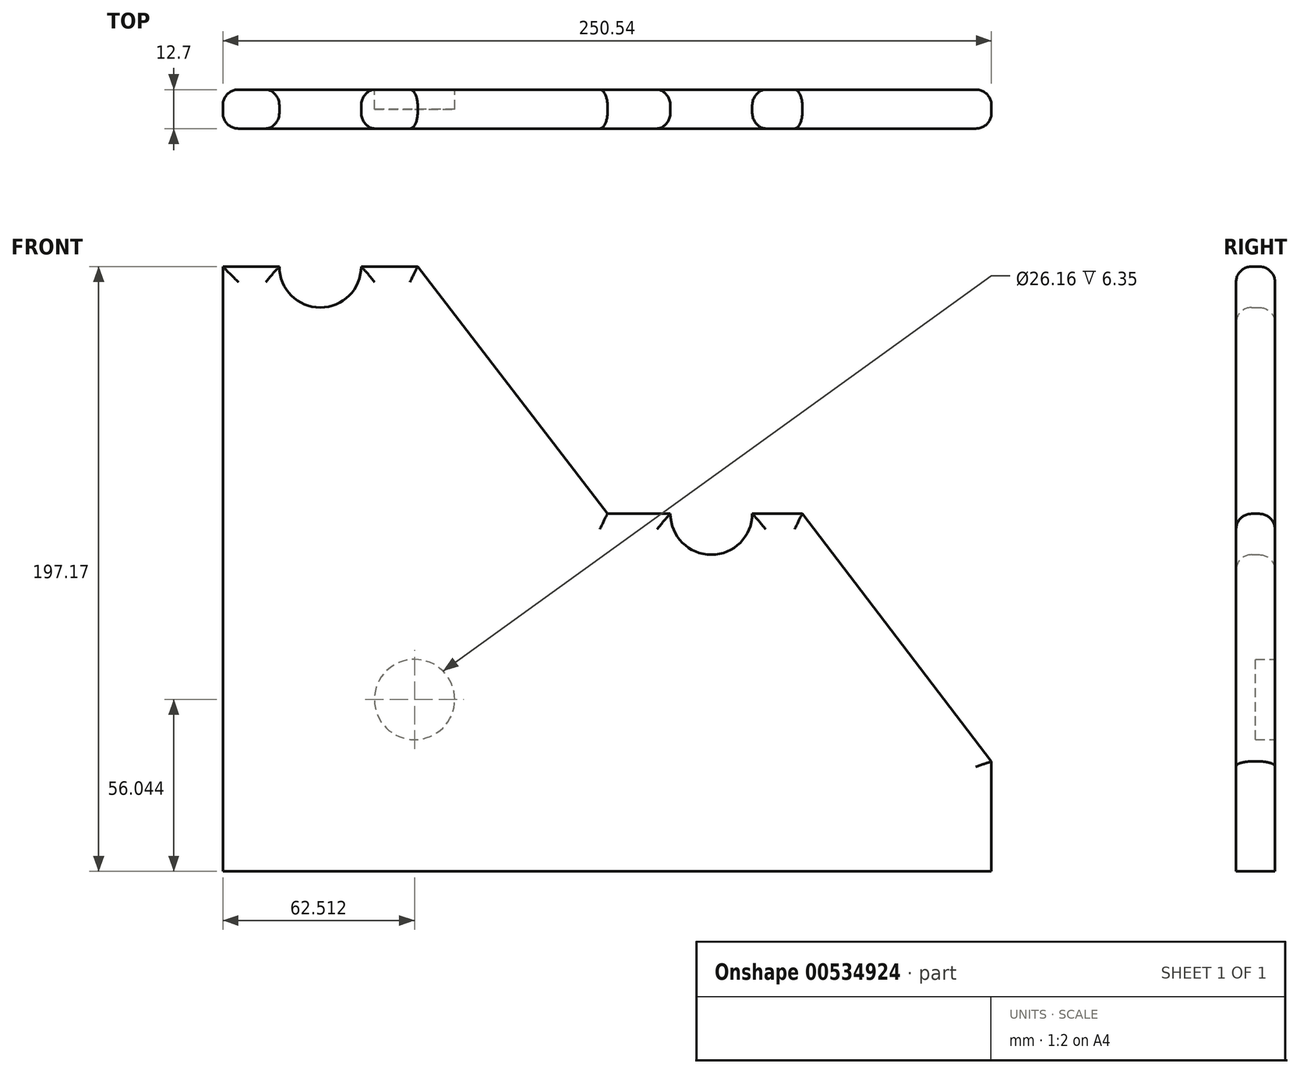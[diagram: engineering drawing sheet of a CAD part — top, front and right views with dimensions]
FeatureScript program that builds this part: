
annotation { "Feature Type Name" : "Feature", "Feature Type Description" : "" }
export const myFeature = defineFeature(function(context is Context, id is Id, definition is map)
    precondition{}
    {
        {
            var Q0;
            Q0=qCreatedBy(makeId("Front.planeOp"),FACE);
            var sketch = newSketch(context, id + "F0", { "sketchPlane" : qUnion([Q0])});
            skLineSegment(sketch, "E0", {"start": v(0, 0) * mm, "end": v(250.54, 0) * mm});
            skLineSegment(sketch, "E1", {"start": v(250.54, 0) * mm, "end": v(250.54, 41.87) * mm});
            skLineSegment(sketch, "E2", {"start": v(250.54, 41.87) * mm, "end": v(188.86, 122.6) * mm});
            skLineSegment(sketch, "E3", {"start": v(188.86, 122.6) * mm, "end": v(172.56, 122.6) * mm});
            skLineSegment(sketch, "E4", {"start": v(125.36, 122.6) * mm, "end": v(63.5, 203.2) * mm});
            skLineSegment(sketch, "E5", {"start": v(63.5, 203.2) * mm, "end": v(45.09, 203.2) * mm});
            skLineSegment(sketch, "E6", {"start": v(0, 203.2) * mm, "end": v(0, 0) * mm});
            skArc(sketch, "E7", {"start": v(145.9, 122.6) * mm, "mid": v(159.23, 109.27) * mm, "end": v(172.56, 122.6) * mm});
            skArc(sketch, "E8", {"start": v(18.41, 203.2) * mm, "mid": v(31.75, 189.86) * mm, "end": v(45.09, 203.2) * mm});
            skLineSegment(sketch, "E9.trimOffspring", {"start": v(18.41, 203.2) * mm, "end": v(0, 203.2) * mm});
            skLineSegment(sketch, "E10.trimOffspring", {"start": v(145.9, 122.6) * mm, "end": v(125.36, 122.6) * mm});
            skSolve(sketch);
        }
        {
            var Q0;
            Q0=makeQuery(id+"F0.imprint","IMPRINT",FACE,{"disambiguationData":[TD([[makeQuery(id+"F0.imprint","IMPRINT",EDGE,{"derivedFrom":sQuery(id+"F0.wireOp",EDGE,"E0")}),1.0]])]});
            extrude(context, id + "F1", {"entities" : qUnion([Q0]), "depth" : 12.7 * mm, "offsetDistance" : 25.4 * mm});
        }
        {
            var Q0;
            Q0=makeQuery(id+"F1.opExtrude","CAP_FACE",FACE,{"disambiguationData":[OSD([sQuery(id+"F0.wireOp",EDGE,"E0"),sQuery(id+"F0.wireOp",EDGE,"E1"),sQuery(id+"F0.wireOp",EDGE,"E2"),sQuery(id+"F0.wireOp",EDGE,"E3"),sQuery(id+"F0.wireOp",EDGE,"E4"),sQuery(id+"F0.wireOp",EDGE,"E5"),sQuery(id+"F0.wireOp",EDGE,"E6"),sQuery(id+"F0.wireOp",EDGE,"E7"),sQuery(id+"F0.wireOp",EDGE,"E8"),sQuery(id+"F0.wireOp",EDGE,"E9.trimOffspring"),sQuery(id+"F0.wireOp",EDGE,"E10.trimOffspring")])],"isStart":false});
            var Q1;
            Q1=makeQuery(id+"F1.opExtrude","CAP_FACE",FACE,{"disambiguationData":[OSD([sQuery(id+"F0.wireOp",EDGE,"E0"),sQuery(id+"F0.wireOp",EDGE,"E1"),sQuery(id+"F0.wireOp",EDGE,"E2"),sQuery(id+"F0.wireOp",EDGE,"E3"),sQuery(id+"F0.wireOp",EDGE,"E4"),sQuery(id+"F0.wireOp",EDGE,"E5"),sQuery(id+"F0.wireOp",EDGE,"E6"),sQuery(id+"F0.wireOp",EDGE,"E7"),sQuery(id+"F0.wireOp",EDGE,"E8"),sQuery(id+"F0.wireOp",EDGE,"E9.trimOffspring"),sQuery(id+"F0.wireOp",EDGE,"E10.trimOffspring")])],"isStart":true});
            fillet(context, id + "F2", {"entities" : qUnion([Q0, Q1]), "radius" : 5.08 * mm, "tangentPropagation" : true, "allowEdgeOverflow" : false});
        }
        {
            var Q0;
            Q0=qCreatedBy(makeId("Front.planeOp"),FACE);
            var sketch = newSketch(context, id + "F3", { "sketchPlane" : qUnion([Q0])});
            skLineSegment(sketch, "E11.bottom", {"start": v(-108.62, 6.03) * mm, "end": v(293.7, 6.03) * mm});
            skLineSegment(sketch, "E11.top", {"start": v(-108.62, -19.59) * mm, "end": v(293.7, -19.59) * mm});
            skLineSegment(sketch, "E11.left", {"start": v(-108.62, 6.03) * mm, "end": v(-108.62, -19.59) * mm});
            skLineSegment(sketch, "E11.right", {"start": v(293.7, 6.03) * mm, "end": v(293.7, -19.59) * mm});
            skSolve(sketch);
        }
        {
            var Q0;
            Q0=makeQuery(id+"F3.imprint","IMPRINT",FACE,{"disambiguationData":[TD([[makeQuery(id+"F3.imprint","IMPRINT",EDGE,{"derivedFrom":sQuery(id+"F3.wireOp",EDGE,"E11.bottom")}),-1.0]])]});
            extrude(context, id + "F4", {"entities" : qUnion([Q0]), "operationType" : NewBodyOperationType.REMOVE, "endBound" : BoundingType.SYMMETRIC, "oppositeDirection" : true, "depth" : 147.32 * mm, "offsetDistance" : 25.4 * mm});
        }
        {
            var Q0;
            Q0=qCreatedBy(makeId("Front.planeOp"),FACE);
            var sketch = newSketch(context, id + "F5", { "sketchPlane" : qUnion([Q0])});
            skCircle(sketch, "E12", {"center": v(62.51, 62.07) * mm, "radius": 13.08 * mm});
            skSolve(sketch);
        }
        {
            var Q0;
            Q0 = qSketchRegion(id + "F5", true);
            var Q1;
            Q1=sQuery(id+"F5.wireOp",EDGE,"E12");
            extrude(context, id + "F6", {"entities" : qUnion([Q0]), "operationType" : NewBodyOperationType.REMOVE, "surfaceEntities" : qUnion([Q1]), "depth" : 6.35 * mm, "offsetDistance" : 25.4 * mm});
        }
    });
